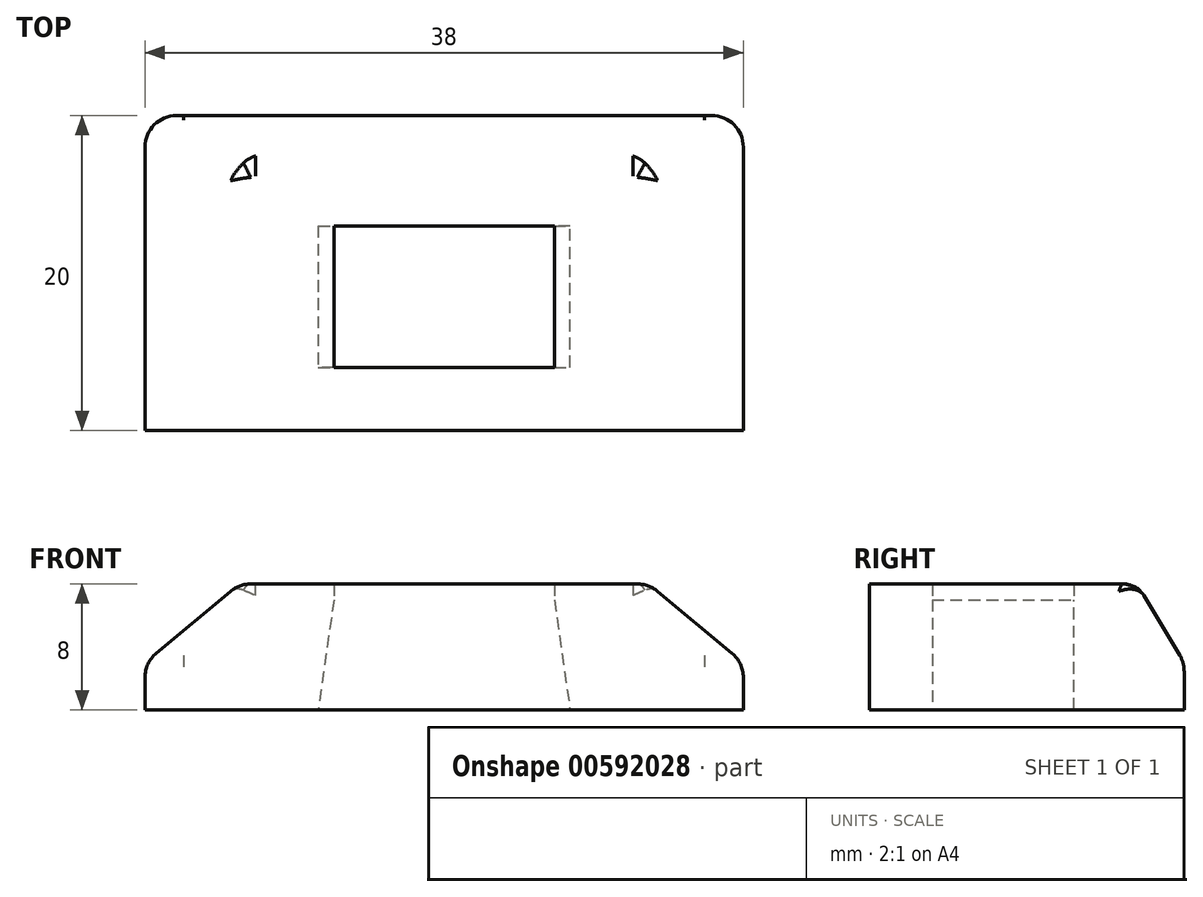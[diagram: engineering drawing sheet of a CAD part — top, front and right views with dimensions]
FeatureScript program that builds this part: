
annotation { "Feature Type Name" : "Feature", "Feature Type Description" : "" }
export const myFeature = defineFeature(function(context is Context, id is Id, definition is map)
    precondition{}
    {
        {
            var Q0;
            Q0=qCreatedBy(makeId("Top.planeOp"),FACE);
            var sketch = newSketch(context, id + "F0", { "sketchPlane" : qUnion([Q0])});
            skLineSegment(sketch, "E0.bottom", {"start": v(-68.98, 0) * mm, "end": v(-30.98, 0) * mm});
            skLineSegment(sketch, "E0.top", {"start": v(-68.98, 20) * mm, "end": v(-30.98, 20) * mm});
            skLineSegment(sketch, "E0.left", {"start": v(-68.98, 0) * mm, "end": v(-68.98, 20) * mm});
            skLineSegment(sketch, "E0.right", {"start": v(-30.98, 0) * mm, "end": v(-30.98, 20) * mm});
            skLineSegment(sketch, "E1.bottom", {"start": v(-56.98, 4) * mm, "end": v(-42.98, 4) * mm});
            skLineSegment(sketch, "E1.top", {"start": v(-56.98, 13) * mm, "end": v(-42.98, 13) * mm});
            skLineSegment(sketch, "E1.left", {"start": v(-56.98, 4) * mm, "end": v(-56.98, 13) * mm});
            skLineSegment(sketch, "E1.right", {"start": v(-42.98, 4) * mm, "end": v(-42.98, 13) * mm});
            skPoint(sketch, "E2", {"position": v(-49.98, 13) * mm});
            skSolve(sketch);
        }
        {
            var Q0;
            Q0=makeQuery(id+"F0.imprint","IMPRINT",FACE,{"disambiguationData":[TD([[makeQuery(id+"F0.imprint","IMPRINT",EDGE,{"derivedFrom":sQuery(id+"F0.wireOp",EDGE,"E0.bottom")}),1.0]])]});
            extrude(context, id + "F1", {"entities" : qUnion([Q0]), "depth" : 8 * mm, "offsetDistance" : 25 * mm});
        }
        {
            var Q0;
            Q0=makeQuery(id+"F1.opExtrude","CAP_EDGE",EDGE,{"disambiguationData":[OSD([sQuery(id+"F0.wireOp",EDGE,"E0.right")])],"isStart":false});
            var Q1;
            Q1=makeQuery(id+"F1.opExtrude","CAP_EDGE",EDGE,{"disambiguationData":[OSD([sQuery(id+"F0.wireOp",EDGE,"E0.left")])],"isStart":false});
            chamfer(context, id + "F2", {"entities" : qUnion([Q0, Q1]), "chamferType" : ChamferType.TWO_OFFSETS, "width1" : 6 * mm, "oppositeDirection" : false, "width2" : 5 * mm, "tangentPropagation" : true});
        }
        {
            var Q0;
            Q0=makeQuery(id+"F1.opExtrude","CAP_EDGE",EDGE,{"disambiguationData":[OSD([sQuery(id+"F0.wireOp",EDGE,"E0.top")])],"isStart":false});
            chamfer(context, id + "F3", {"entities" : qUnion([Q0]), "chamferType" : ChamferType.TWO_OFFSETS, "width1" : 5 * mm, "oppositeDirection" : false, "width2" : 3 * mm, "tangentPropagation" : true});
        }
        {
            var Q0;
            {var subQ0=sQuery(id+"F0.wireOp",EDGE,"E0.top");Q0=makeQuery(id+"F3.opChamfer","BLEND_EDGE",EDGE,{"blendedFrom":[makeQuery(id+"F1.opExtrude","CAP_EDGE",EDGE,{"disambiguationData":[OSD([subQ0])],"isStart":false}),makeQuery(id+"F1.opExtrude","SWEPT_FACE",FACE,{"disambiguationData":[OSD([subQ0])]})],"blendedInto":[makeQuery(id+"F1.opExtrude","SWEPT_FACE",FACE,{"disambiguationData":[OSD([subQ0])]})]});}
            var Q1;
            {var subQ0=sQuery(id+"F0.wireOp",EDGE,"E0.left");Q1=makeQuery(id+"F2.opChamfer","BLEND_EDGE",EDGE,{"blendedFrom":[makeQuery(id+"F1.opExtrude","CAP_EDGE",EDGE,{"disambiguationData":[OSD([subQ0])],"isStart":false}),makeQuery(id+"F1.opExtrude","SWEPT_FACE",FACE,{"disambiguationData":[OSD([subQ0])]})],"blendedInto":[makeQuery(id+"F1.opExtrude","SWEPT_FACE",FACE,{"disambiguationData":[OSD([subQ0])]})]});}
            var Q2;
            {var subQ0=sQuery(id+"F0.wireOp",EDGE,"E0.right");Q2=makeQuery(id+"F2.opChamfer","BLEND_EDGE",EDGE,{"blendedFrom":[makeQuery(id+"F1.opExtrude","CAP_EDGE",EDGE,{"disambiguationData":[OSD([subQ0])],"isStart":false}),makeQuery(id+"F1.opExtrude","SWEPT_FACE",FACE,{"disambiguationData":[OSD([subQ0])]})],"blendedInto":[makeQuery(id+"F1.opExtrude","SWEPT_FACE",FACE,{"disambiguationData":[OSD([subQ0])]})]});}
            fillet(context, id + "F4", {"entities" : qUnion([Q0, Q1, Q2]), "tangentPropagation" : true, "radius" : 2 * mm, "defaultsChanged" : false, "vertexSettings" : [], "allowEdgeOverflow" : false});
        }
        {
            var Q0;
            {var subQ0=sQuery(id+"F0.wireOp",EDGE,"E0.top");Q0=makeQuery(id+"F3.opChamfer","BLEND_EDGE",EDGE,{"blendedFrom":[makeQuery(id+"F1.opExtrude","CAP_EDGE",EDGE,{"disambiguationData":[OSD([subQ0])],"isStart":false}),makeQuery(id+"F1.opExtrude","CAP_FACE",FACE,{"disambiguationData":[OSD([sQuery(id+"F0.wireOp",EDGE,"E0.bottom"),subQ0,sQuery(id+"F0.wireOp",EDGE,"E0.left"),sQuery(id+"F0.wireOp",EDGE,"E0.right"),sQuery(id+"F0.wireOp",EDGE,"E1.bottom"),sQuery(id+"F0.wireOp",EDGE,"E1.top"),sQuery(id+"F0.wireOp",EDGE,"E1.left"),sQuery(id+"F0.wireOp",EDGE,"E1.right")])],"isStart":false})],"blendedInto":[makeQuery(id+"F1.opExtrude","CAP_FACE",FACE,{"disambiguationData":[OSD([sQuery(id+"F0.wireOp",EDGE,"E0.bottom"),subQ0,sQuery(id+"F0.wireOp",EDGE,"E0.left"),sQuery(id+"F0.wireOp",EDGE,"E0.right"),sQuery(id+"F0.wireOp",EDGE,"E1.bottom"),sQuery(id+"F0.wireOp",EDGE,"E1.top"),sQuery(id+"F0.wireOp",EDGE,"E1.left"),sQuery(id+"F0.wireOp",EDGE,"E1.right")])],"isStart":false})]});}
            fillet(context, id + "F5", {"entities" : qUnion([Q0]), "tangentPropagation" : true, "radius" : 1.5 * mm, "defaultsChanged" : true, "vertexSettings" : [], "allowEdgeOverflow" : false});
        }
        {
            var Q0;
            Q0=makeQuery(id+"F3.opChamfer","BLEND_EDGE",EDGE,{"blendedFrom":[makeQuery(id+"F1.opExtrude","CAP_EDGE",EDGE,{"disambiguationData":[OSD([sQuery(id+"F0.wireOp",EDGE,"E0.top")])],"isStart":false}),makeQuery(id+"F2.opChamfer","BLEND_FACE",FACE,{"disambiguationData":[OSD([sQuery(id+"F0.wireOp",EDGE,"E0.right")])]})],"blendedInto":[makeQuery(id+"F2.opChamfer","BLEND_FACE",FACE,{"disambiguationData":[OSD([sQuery(id+"F0.wireOp",EDGE,"E0.right")])]})]});
            var Q1;
            Q1=makeQuery(id+"F1.opExtrude","SWEPT_EDGE",EDGE,{"disambiguationData":[OSD([sQuery(id+"F0.wireOp",EDGE,"E0.top"),sQuery(id+"F0.wireOp",EDGE,"E0.right")])]});
            var Q2;
            Q2=makeQuery(id+"F3.opChamfer","BLEND_EDGE",EDGE,{"blendedFrom":[makeQuery(id+"F1.opExtrude","CAP_EDGE",EDGE,{"disambiguationData":[OSD([sQuery(id+"F0.wireOp",EDGE,"E0.top")])],"isStart":false}),makeQuery(id+"F2.opChamfer","BLEND_FACE",FACE,{"disambiguationData":[OSD([sQuery(id+"F0.wireOp",EDGE,"E0.left")])]})],"blendedInto":[makeQuery(id+"F2.opChamfer","BLEND_FACE",FACE,{"disambiguationData":[OSD([sQuery(id+"F0.wireOp",EDGE,"E0.left")])]})]});
            var Q3;
            Q3=makeQuery(id+"F1.opExtrude","SWEPT_EDGE",EDGE,{"disambiguationData":[OSD([sQuery(id+"F0.wireOp",EDGE,"E0.top"),sQuery(id+"F0.wireOp",EDGE,"E0.left")])]});
            fillet(context, id + "F6", {"entities" : qUnion([Q0, Q1, Q2, Q3]), "tangentPropagation" : true, "radius" : 2 * mm, "defaultsChanged" : false, "vertexSettings" : [], "allowEdgeOverflow" : false});
        }
        {
            var Q0;
            Q0=makeQuery(id+"F1.opExtrude","CAP_EDGE",EDGE,{"disambiguationData":[OSD([sQuery(id+"F0.wireOp",EDGE,"E1.right")])],"isStart":true});
            var Q1;
            Q1=makeQuery(id+"F1.opExtrude","CAP_EDGE",EDGE,{"disambiguationData":[OSD([sQuery(id+"F0.wireOp",EDGE,"E1.left")])],"isStart":true});
            chamfer(context, id + "F7", {"entities" : qUnion([Q0, Q1]), "chamferType" : ChamferType.TWO_OFFSETS, "width1" : 7 * mm, "oppositeDirection" : true, "width2" : 1 * mm, "tangentPropagation" : true});
        }
    });
